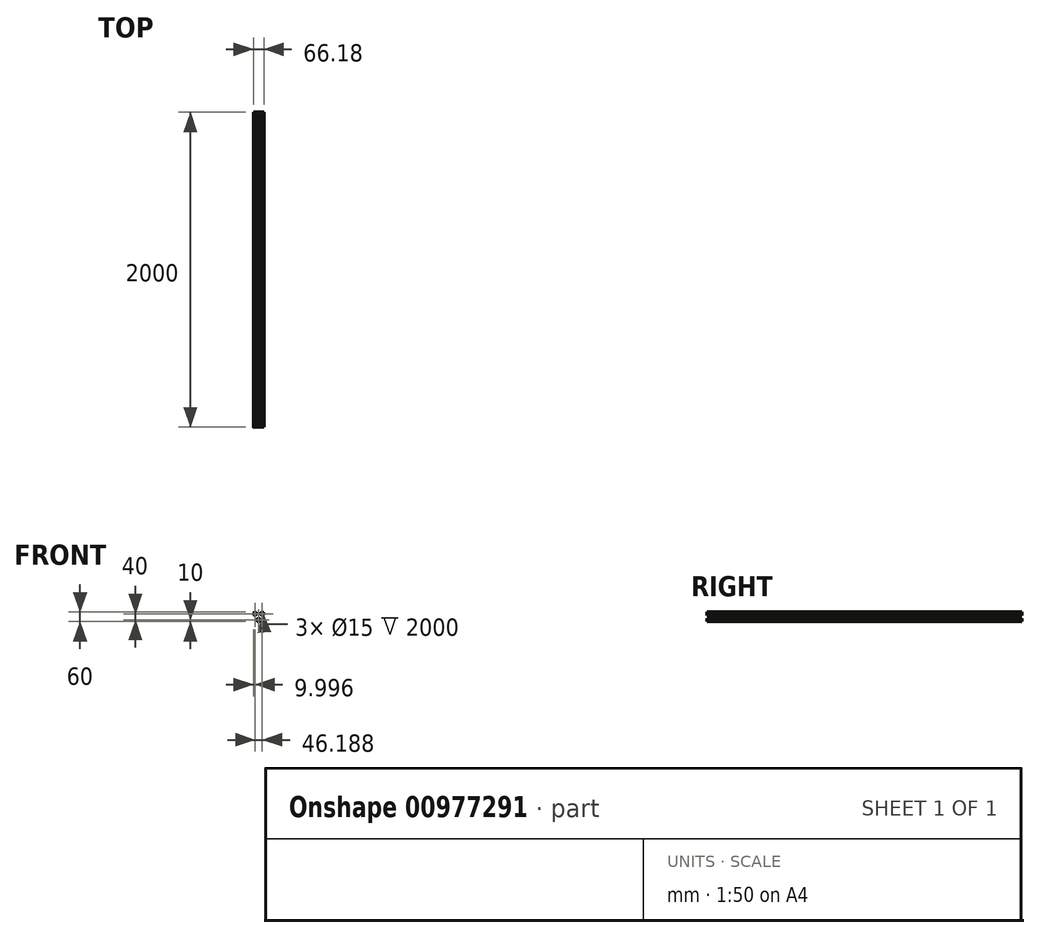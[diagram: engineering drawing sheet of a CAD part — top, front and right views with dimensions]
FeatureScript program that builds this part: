
annotation { "Feature Type Name" : "Feature", "Feature Type Description" : "" }
export const myFeature = defineFeature(function(context is Context, id is Id, definition is map)
    precondition{}
    {
        {
            var Q0;
            Q0=qCreatedBy(makeId("Front.planeOp"),FACE);
            var sketch = newSketch(context, id + "F0", { "sketchPlane" : qUnion([Q0])});
            skCircle(sketch, "E0", {"center": v(0, 0) * mm, "radius": 10 * mm});
            skCircle(sketch, "E1", {"center": v(23.1, 40) * mm, "radius": 10 * mm});
            skCircle(sketch, "E2", {"center": v(-23.1, 40) * mm, "radius": 10 * mm});
            skCircle(sketch, "E3", {"center": v(-23.1, 40) * mm, "radius": 15 * mm});
            skCircle(sketch, "E4", {"center": v(23.1, 40) * mm, "radius": 15 * mm});
            skCircle(sketch, "E5", {"center": v(0, 0) * mm, "radius": 15 * mm});
            skLineSegment(sketch, "E6", {"start": v(0, 0) * mm, "end": v(-23.1, 40) * mm});
            skLineSegment(sketch, "E7", {"start": v(23.1, 40) * mm, "end": v(0, 0) * mm});
            skLineSegment(sketch, "E8", {"start": v(-23.1, 40) * mm, "end": v(23.1, 40) * mm});
            skCircle(sketch, "E9", {"center": v(23.1, 40) * mm, "radius": 7.5 * mm});
            skCircle(sketch, "E10", {"center": v(-23.1, 40) * mm, "radius": 7.5 * mm});
            skCircle(sketch, "E11", {"center": v(0, 0) * mm, "radius": 7.5 * mm});
            skSolve(sketch);
        }
        {
            var Q0;
            {var subQ0=sQuery(id+"F0.wireOp",EDGE,"E6");var subQ1=sQuery(id+"F0.wireOp",EDGE,"E2");var subQ2=makeQuery(id+"F0.imprint","INTERSECT",VERTEX,{"derivedFrom":[subQ1,subQ0]});Q0=makeQuery(id+"F0.imprint","IMPRINT",FACE,{"disambiguationData":[TD([[makeQuery(id+"F0.imprint","IMPRINT",EDGE,{"disambiguationData":[TD([[subQ2,1.0]])],"derivedFrom":subQ1}),1.0]])]});}
            var Q1;
            {var subQ0=sQuery(id+"F0.wireOp",EDGE,"E6");var subQ1=sQuery(id+"F0.wireOp",EDGE,"E2");var subQ2=makeQuery(id+"F0.imprint","INTERSECT",VERTEX,{"derivedFrom":[subQ1,subQ0]});Q1=makeQuery(id+"F0.imprint","IMPRINT",FACE,{"disambiguationData":[TD([[makeQuery(id+"F0.imprint","IMPRINT",EDGE,{"disambiguationData":[TD([[subQ2,-1.0]])],"derivedFrom":subQ1}),1.0]])]});}
            var Q2;
            {var subQ0=sQuery(id+"F0.wireOp",EDGE,"E7");var subQ1=sQuery(id+"F0.wireOp",EDGE,"E1");var subQ2=makeQuery(id+"F0.imprint","INTERSECT",VERTEX,{"derivedFrom":[subQ1,subQ0]});Q2=makeQuery(id+"F0.imprint","IMPRINT",FACE,{"disambiguationData":[TD([[makeQuery(id+"F0.imprint","IMPRINT",EDGE,{"disambiguationData":[TD([[subQ2,-1.0]])],"derivedFrom":subQ1}),1.0]])]});}
            var Q3;
            {var subQ0=sQuery(id+"F0.wireOp",EDGE,"E7");var subQ1=sQuery(id+"F0.wireOp",EDGE,"E1");var subQ2=makeQuery(id+"F0.imprint","INTERSECT",VERTEX,{"derivedFrom":[subQ1,subQ0]});Q3=makeQuery(id+"F0.imprint","IMPRINT",FACE,{"disambiguationData":[TD([[makeQuery(id+"F0.imprint","IMPRINT",EDGE,{"disambiguationData":[TD([[subQ2,1.0]])],"derivedFrom":subQ1}),1.0]])]});}
            var Q4;
            {var subQ0=sQuery(id+"F0.wireOp",EDGE,"E6");var subQ1=sQuery(id+"F0.wireOp",EDGE,"E0");var subQ2=makeQuery(id+"F0.imprint","INTERSECT",VERTEX,{"derivedFrom":[subQ1,subQ0]});Q4=makeQuery(id+"F0.imprint","IMPRINT",FACE,{"disambiguationData":[TD([[makeQuery(id+"F0.imprint","IMPRINT",EDGE,{"disambiguationData":[TD([[subQ2,1.0]])],"derivedFrom":subQ1}),1.0]])]});}
            var Q5;
            {var subQ0=sQuery(id+"F0.wireOp",EDGE,"E6");var subQ1=sQuery(id+"F0.wireOp",EDGE,"E0");var subQ2=makeQuery(id+"F0.imprint","INTERSECT",VERTEX,{"derivedFrom":[subQ1,subQ0]});Q5=makeQuery(id+"F0.imprint","IMPRINT",FACE,{"disambiguationData":[TD([[makeQuery(id+"F0.imprint","IMPRINT",EDGE,{"disambiguationData":[TD([[subQ2,-1.0]])],"derivedFrom":subQ1}),1.0]])]});}
            extrude(context, id + "F1", {"entities" : qUnion([Q0, Q1, Q2, Q3, Q4, Q5]), "depth" : 2000 * mm, "offsetDistance" : 25 * mm});
        }
    });
